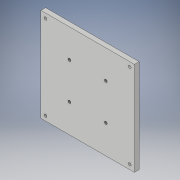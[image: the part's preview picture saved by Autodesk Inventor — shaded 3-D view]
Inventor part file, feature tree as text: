
AUTODESK INVENTOR PART (.ipt)
format: ipt  version: 2017 (Build 210142000, 142)  size: 119,296 bytes
history: native  units: in
note: dims shown in document units (in); Inventor stores cm internally (conversion verified against a paired STEP export)
features: thread x4, extrude x1, sketch x1
ambient origin geometry x8: Origin, YZ Plane, XZ Plane, XY Plane, X Axis, Y Axis, Z Axis, Center Point
bodies: Body1 (feature_tree)
feature tree (6):
  extrude  "Extrusion2"  Depth=0.3937in
  thread  "Thread1"  [1 undecoded]
  thread  "Thread2"  [1 undecoded]
  thread  "Thread3"  [1 undecoded]
  thread  "Thread4"  [1 undecoded]
  sketch  "Sketch1"  dims[d1=7.874in d5=0.3937in d6=0.3937in d7=0.3937in d8=0.3937in d9=0.2362in d10=0.2362in d11=0.3937in d12=0.3937in d14=0.3937in d15=0.2362in d16=0.2362in d17=0.2362in d18=0.2362in d19=0.2362in d20=0.2362in d32=0.3937in d33=0.0in d34=0.3937in d35=0.0in d36=0.3937in d37=0.0in d38=0.3937in d39=0.0in d40=0.3937in d41=0.0in d42=7.874in d43=0.3937in]
note: 4 required parameter values undecoded (feature->parameter linkage not recoverable at this tier; creation-order binding heuristic only, values carry confidence <= 0.55)
